# Revit family: TD92_CUK124_BRA010_RVT20_R00
name_source: partatom
category: Mobiliário
units: mm (PartAtom-declared; Revit-internal decimal feet)

## family parameters
Com base no plano de trabalho = Não
Compartilhado = Não
Corte com vazios quando carregada = Não
Número OmniClass = 23.40.20.00
Ponto de cálculo do ambiente = Não
Sempre na vertical = Sim
Título OmniClass = General Furniture and Specialties

## types (1)
- TD92_CUK124_BRA010_RVT20_R00
    Descrição = Através dos brinquedos as crianças se divertem e aprendem. Com a Gangorra Infantil Tramontina Cuckoo em Polietileno da linha Infantil, a diversão e o aprendizado estarão garantidos! O Cuckoo é uma gangorra única, que conta com um visual de passarinho para estimular a criatividade e imaginação. Além disso, os papais podem ficar tranquilos, pois a gangorra Cuckoo é leve, sendo produzida em polietileno e totalmente livre de material tóxico. E como a diversão sempre acompanha as crianças, a gangorra é compacta e fácil de transportar.
    Elevação padrão = 0  [stored 0 ft]
    Fabricante = Tramontina Delta S/A
    Modelo = Gangorra Infantil Tramontina Cuckoo em Polietileno Branco
    Nota-chave = 92124010
    URL = https://www.tramontinastore.com

note: [stored X ft] marks values corroborated as IEEE doubles in the binary element streams (Revit-internal decimal feet)
